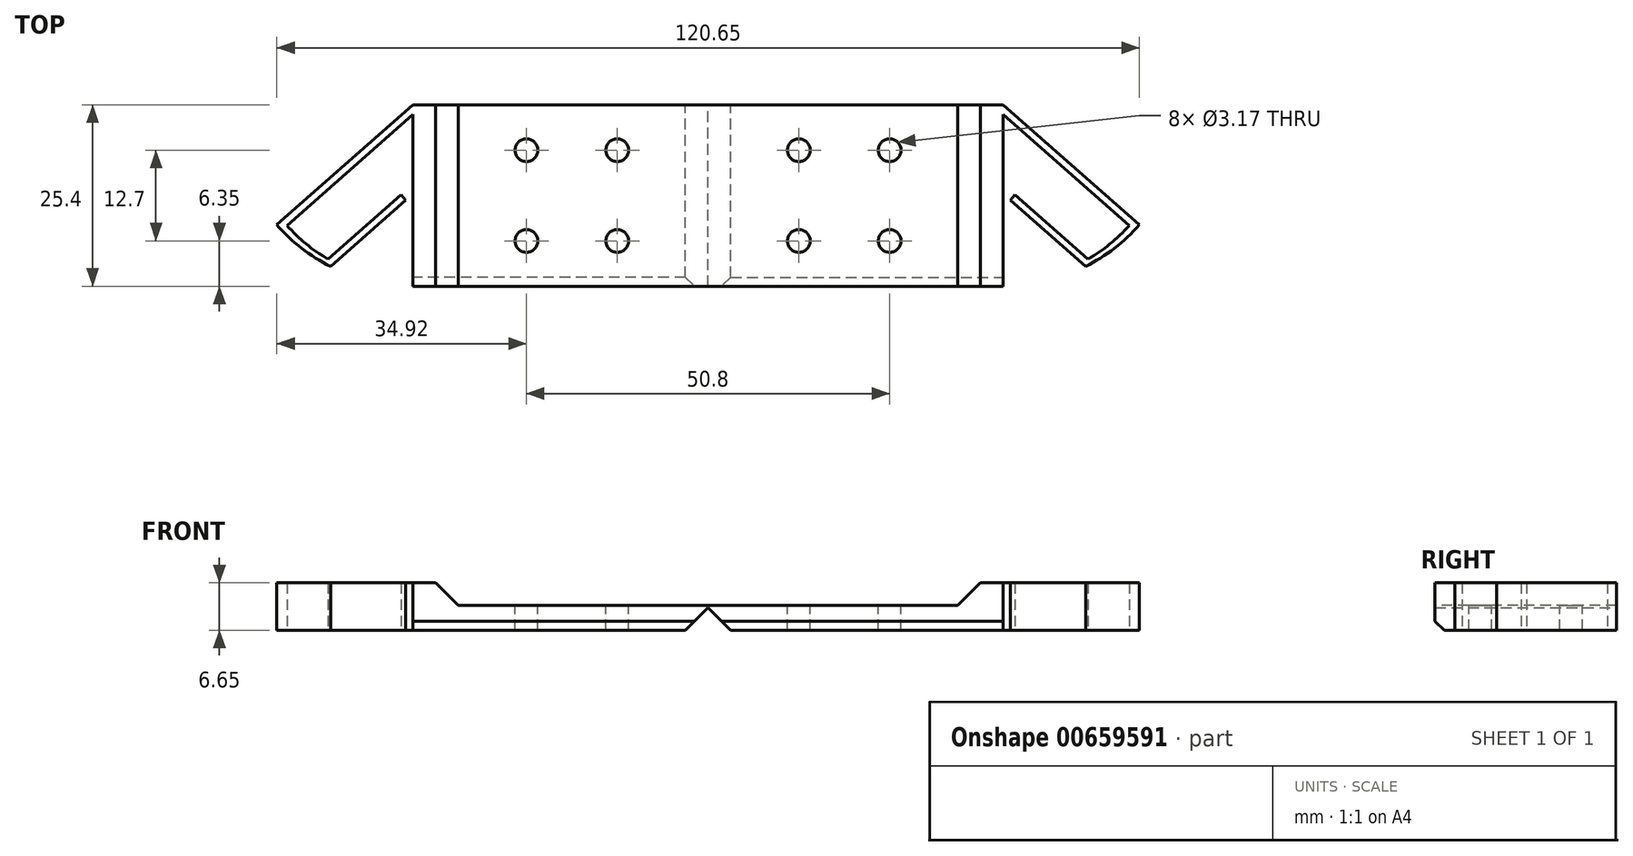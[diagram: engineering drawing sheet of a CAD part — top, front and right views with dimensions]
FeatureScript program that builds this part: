
annotation { "Feature Type Name" : "Feature", "Feature Type Description" : "" }
export const myFeature = defineFeature(function(context is Context, id is Id, definition is map)
    precondition{}
    {
        {
            var Q0;
            Q0=qCreatedBy(makeId("Top.planeOp"),FACE);
            var sketch = newSketch(context, id + "F0", { "sketchPlane" : qUnion([Q0])});
            skLineSegment(sketch, "E0.bottom", {"start": v(28.58, -12.7) * mm, "end": v(-28.58, -12.7) * mm});
            skLineSegment(sketch, "E0.top", {"start": v(28.58, 12.7) * mm, "end": v(-28.58, 12.7) * mm});
            skLineSegment(sketch, "E0.left", {"start": v(28.58, -12.7) * mm, "end": v(28.58, 12.7) * mm});
            skLineSegment(sketch, "E0.right", {"start": v(-28.57, -12.7) * mm, "end": v(-28.57, 12.7) * mm});
            skPoint(sketch, "E0.middle", {"position": v(0, 0) * mm});
            skLineSegment(sketch, "E1", {"start": v(-9.53, 11.37) * mm, "end": v(-9.52, -12.7) * mm});
            skLineSegment(sketch, "E2", {"start": v(0, -12.7) * mm, "end": v(0, 12.7) * mm});
            skPoint(sketch, "E3", {"position": v(-22.22, -12.7) * mm});
            skLineSegment(sketch, "E4", {"start": v(-9.53, 12.7) * mm, "end": v(-28.57, -4.1) * mm});
            skPoint(sketch, "E5", {"position": v(-19.05, -12.7) * mm});
            skArc(sketch, "E6", {"start": v(-28.57, -4.1) * mm, "mid": v(-25.09, -7.37) * mm, "end": v(-21.05, -9.94) * mm});
            skLineSegment(sketch, "E7", {"start": v(-21.05, -9.94) * mm, "end": v(-10.53, -0.66) * mm});
            skLineSegment(sketch, "E8", {"start": v(-10.53, -0.66) * mm, "end": v(-11.19, 0.1) * mm});
            skLineSegment(sketch, "E9", {"start": v(-11.19, 0.1) * mm, "end": v(-11.19, 0.1) * mm});
            skLineSegment(sketch, "E10", {"start": v(-9.53, 11.37) * mm, "end": v(-27.15, -4.18) * mm});
            skArc(sketch, "E11", {"start": v(-27.15, -4.18) * mm, "mid": v(-24.46, -6.77) * mm, "end": v(-21.4, -8.91) * mm});
            skLineSegment(sketch, "E12", {"start": v(-21.4, -8.91) * mm, "end": v(-11.19, 0.1) * mm});
            skSolve(sketch);
        }
        {
            var Q0;
            {var subQ0=sQuery(id+"F0.wireOp",EDGE,"E0.left");Q0=makeQuery(id+"F0.imprint","IMPRINT",FACE,{"disambiguationData":[TD([[makeQuery(id+"F0.imprint","IMPRINT",EDGE,{"derivedFrom":subQ0}),1.0]])]});}
            var Q1;
            {var subQ1=sQuery(id+"F0.wireOp",EDGE,"E1");Q1=makeQuery(id+"F0.imprint","IMPRINT",FACE,{"disambiguationData":[TD([[makeQuery(id+"F0.imprint","IMPRINT",EDGE,{"derivedFrom":subQ1}),1.0]])]});}
            var Q2;
            {var subQ0=sQuery(id+"F0.wireOp",EDGE,"Ll8NUgnO-918t-zldm-zNWz-RsUZQomu35K8");Q2=makeQuery(id+"F0.imprint","IMPRINT",FACE,{"disambiguationData":[TD([[makeQuery(id+"F0.imprint","IMPRINT",EDGE,{"derivedFrom":subQ0}),1.0]])]});}
            extrude(context, id + "F1", {"entities" : qUnion([Q0, Q1, Q2]), "depth" : 3.17 * mm, "offsetDistance" : 25.4 * mm});
        }
        {
            var Q0;
            {var subQ1=sQuery(id+"F0.wireOp",EDGE,"E1");Q0=makeQuery(id+"F0.imprint","IMPRINT",FACE,{"disambiguationData":[TD([[makeQuery(id+"F0.imprint","IMPRINT",EDGE,{"derivedFrom":subQ1}),1.0]])]});}
            extrude(context, id + "F2", {"entities" : qUnion([Q0]), "operationType" : NewBodyOperationType.ADD, "depth" : 6.35 * mm, "offsetDistance" : 25.4 * mm});
        }
        {
            var Q0;
            Q0=makeQuery(id+"F2.opExtrude","CAP_EDGE",EDGE,{"disambiguationData":[OSD([sQuery(id+"F0.wireOp",EDGE,"E2")])],"isStart":false});
            chamfer(context, id + "F3", {"entities" : qUnion([Q0]), "width" : 6.35 * mm, "tangentPropagation" : true});
        }
        {
            var Q0;
            {var subQ0=sQuery(id+"F0.wireOp",EDGE,"E0.left");Q0=makeQuery(id+"F37SAEC6IVc2ddh_1.boolean.opBoolean","MERGE",FACE,{"derivedFrom":[makeQuery(id+"F1.opExtrude","SWEPT_FACE",FACE,{"disambiguationData":[OSD([subQ0])]}),makeQuery(id+"F37SAEC6IVc2ddh_1.opExtrude","SWEPT_FACE",FACE,{"disambiguationData":[OSD([subQ0])]})]});}
            cPlane(context, id + "F4", {"entities" : qUnion([Q0]), "cplaneType" : CPlaneType.OFFSET, "offset" : 3.17 * mm, "width" : 152.4 * mm, "height" : 152.4 * mm});
        }
        {
            var Q0;
            {var subQ0=sQuery(id+"F0.wireOp",EDGE,"E1");Q0=makeQuery(id+"F2.boolean.opBoolean","MERGE",FACE,{"derivedFrom":[makeQuery(id+"F1.opExtrude","SWEPT_FACE",FACE,{"disambiguationData":[OSD([subQ0])]}),makeQuery(id+"F2.opExtrude","SWEPT_FACE",FACE,{"disambiguationData":[OSD([subQ0])]})]});}
            var sketch = newSketch(context, id + "F5", { "sketchPlane" : qUnion([Q0])});
            skLineSegment(sketch, "E13", {"start": v(12.7, 0) * mm, "end": v(12.7, 1.27) * mm});
            skLineSegment(sketch, "E14", {"start": v(12.7, 1.27) * mm, "end": v(11.43, 0) * mm});
            skLineSegment(sketch, "E15", {"start": v(11.43, 0) * mm, "end": v(12.7, 0) * mm});
            skSolve(sketch);
        }
        {
            var Q0;
            {var subQ0=sQuery(id+"F0.wireOp",EDGE,"E0.top");Q0=makeQuery(id+"F2.boolean.opBoolean","MERGE",FACE,{"derivedFrom":[makeQuery(id+"F1.opExtrude","SWEPT_FACE",FACE,{"disambiguationData":[OSD([subQ0])]}),makeQuery(id+"F2.opExtrude","SWEPT_FACE",FACE,{"disambiguationData":[OSD([subQ0])]})]});}
            var sketch = newSketch(context, id + "F6", { "sketchPlane" : qUnion([Q0])});
            skLineSegment(sketch, "E16", {"start": v(-28.58, 3.18) * mm, "end": v(-31.75, 3.18) * mm});
            skLineSegment(sketch, "E17", {"start": v(-31.75, 3.18) * mm, "end": v(-28.58, 0) * mm});
            skLineSegment(sketch, "E18", {"start": v(-28.58, 0) * mm, "end": v(-28.58, 3.18) * mm});
            skSolve(sketch);
        }
        {
            var Q0;
            Q0=makeQuery(id+"F6.imprint","IMPRINT",FACE,{"disambiguationData":[TD([[makeQuery(id+"F6.imprint","IMPRINT",EDGE,{"derivedFrom":sQuery(id+"F6.wireOp",EDGE,"E18")}),1.0]])]});
            var Q1;
            Q1=makeQuery(id+"F6.imprint","IMPRINT",FACE,{"disambiguationData":[TD([[makeQuery(id+"F6.imprint","IMPRINT",EDGE,{"derivedFrom":sQuery(id+"F6.wireOp",EDGE,"E16")}),1.0]])]});
            extrude(context, id + "F7", {"entities" : qUnion([Q0, Q1]), "operationType" : NewBodyOperationType.ADD, "oppositeDirection" : true, "depth" : 25.4 * mm, "offsetDistance" : 25.4 * mm});
        }
        {
            var Q0;
            Q0=makeQuery(id+"F5.imprint","IMPRINT",FACE,{"disambiguationData":[TD([[makeQuery(id+"F5.imprint","IMPRINT",EDGE,{"derivedFrom":sQuery(id+"F5.wireOp",EDGE,"E13")}),-1.0]])]});
            extrude(context, id + "F8", {"entities" : qUnion([Q0]), "operationType" : NewBodyOperationType.REMOVE, "oppositeDirection" : true, "depth" : 50.8 * mm, "offsetDistance" : 25.4 * mm});
        }
        {
            var Q0;
            Q0=makeQuery(id+"F1.opExtrude","SWEPT_BODY",BODY,{"disambiguationData":[OSD([sQuery(id+"F0.wireOp",EDGE,"E0.bottom"),sQuery(id+"F0.wireOp",EDGE,"E0.top"),sQuery(id+"F0.wireOp",EDGE,"E0.left"),sQuery(id+"F0.wireOp",EDGE,"E1"),sQuery(id+"F0.wireOp",EDGE,"E4"),sQuery(id+"F0.wireOp",EDGE,"E6"),sQuery(id+"F0.wireOp",EDGE,"E7"),sQuery(id+"F0.wireOp",EDGE,"E8"),sQuery(id+"F0.wireOp",EDGE,"E10"),sQuery(id+"F0.wireOp",EDGE,"E11"),sQuery(id+"F0.wireOp",EDGE,"E12")])]});
            var Q1;
            Q1=qCreatedBy(id+"F4.planeOp",FACE);
            mirror(context, id + "F9", {"entities" : qUnion([Q0]), "mirrorPlane" : qUnion([Q1])});
        }
        {
            var Q0;
            {var subQ0=sQuery(id+"F0.wireOp",EDGE,"E0.top");Q0=makeQuery(id+"F7.boolean.opBoolean","MERGE",FACE,{"derivedFrom":[makeQuery(id+"F1.opExtrude","CAP_FACE",FACE,{"disambiguationData":[OSD([sQuery(id+"F0.wireOp",EDGE,"E0.bottom"),subQ0,sQuery(id+"F0.wireOp",EDGE,"E0.left"),sQuery(id+"F0.wireOp",EDGE,"E1"),sQuery(id+"F0.wireOp",EDGE,"E4"),sQuery(id+"F0.wireOp",EDGE,"E6"),sQuery(id+"F0.wireOp",EDGE,"E7"),sQuery(id+"F0.wireOp",EDGE,"E8"),sQuery(id+"F0.wireOp",EDGE,"E10"),sQuery(id+"F0.wireOp",EDGE,"E11"),sQuery(id+"F0.wireOp",EDGE,"E12")])],"isStart":false}),makeQuery(id+"F7.opExtrude","SWEPT_FACE",FACE,{"disambiguationData":[OSD([subQ0,sQuery(id+"F6.wireOp",EDGE,"E16")])]})]});}
            var sketch = newSketch(context, id + "F10", { "sketchPlane" : qUnion([Q0])});
            skLineSegment(sketch, "E19", {"start": v(31.75, 0) * mm, "end": v(19.05, 0) * mm, "construction": true});
            skPoint(sketch, "E19.endSnap0", {"position": v(-3.17, 0) * mm});
            skLineSegment(sketch, "E20", {"start": v(19.05, 0) * mm, "end": v(6.35, 0) * mm, "construction": true});
            skLineSegment(sketch, "E21", {"start": v(6.35, 0) * mm, "end": v(6.35, 0) * mm});
            skLineSegment(sketch, "E22", {"start": v(31.75, 0) * mm, "end": v(44.45, 0) * mm, "construction": true});
            skLineSegment(sketch, "E23", {"start": v(44.45, 0) * mm, "end": v(57.15, 0) * mm, "construction": true});
            skLineSegment(sketch, "E24.bottom", {"start": v(44.45, 6.35) * mm, "end": v(19.05, 6.35) * mm, "construction": true});
            skLineSegment(sketch, "E24.top", {"start": v(44.45, -6.35) * mm, "end": v(19.05, -6.35) * mm, "construction": true});
            skLineSegment(sketch, "E24.left", {"start": v(44.45, 6.35) * mm, "end": v(44.45, -6.35) * mm, "construction": true});
            skLineSegment(sketch, "E24.right", {"start": v(19.05, 6.35) * mm, "end": v(19.05, -6.35) * mm, "construction": true});
            skPoint(sketch, "E24.middle", {"position": v(31.75, 0) * mm});
            skLineSegment(sketch, "E25.bottom", {"start": v(57.15, 6.35) * mm, "end": v(6.35, 6.35) * mm, "construction": true});
            skLineSegment(sketch, "E25.top", {"start": v(57.15, -6.35) * mm, "end": v(6.35, -6.35) * mm, "construction": true});
            skLineSegment(sketch, "E25.left", {"start": v(57.15, 6.35) * mm, "end": v(57.15, -6.35) * mm, "construction": true});
            skLineSegment(sketch, "E25.right", {"start": v(6.35, 6.35) * mm, "end": v(6.35, -6.35) * mm, "construction": true});
            skSolve(sketch);
        }
        {
            var Q0;
            Q0=sQuery(id+"F10.wireOp",VERTEX,"E25.left.end");
            var Q1;
            Q1=sQuery(id+"F10.wireOp",VERTEX,"E25.bottom.start");
            var Q2;
            Q2=sQuery(id+"F10.wireOp",VERTEX,"E24.bottom.end");
            var Q3;
            Q3=sQuery(id+"F10.wireOp",VERTEX,"E24.right.end");
            var Q4;
            Q4=sQuery(id+"F10.wireOp",VERTEX,"E25.right.end");
            var Q5;
            Q5=sQuery(id+"F10.wireOp",VERTEX,"E25.bottom.end");
            var Q6;
            Q6=sQuery(id+"F10.wireOp",VERTEX,"E24.top.start");
            var Q7;
            Q7=sQuery(id+"F10.wireOp",VERTEX,"E24.bottom.start");
            var Q8;
            Q8=makeQuery(id+"F1.opExtrude","SWEPT_BODY",BODY,{"disambiguationData":[OSD([sQuery(id+"F0.wireOp",EDGE,"E0.bottom"),sQuery(id+"F0.wireOp",EDGE,"E0.top"),sQuery(id+"F0.wireOp",EDGE,"E0.left"),sQuery(id+"F0.wireOp",EDGE,"E1"),sQuery(id+"F0.wireOp",EDGE,"E4"),sQuery(id+"F0.wireOp",EDGE,"E6"),sQuery(id+"F0.wireOp",EDGE,"E7"),sQuery(id+"F0.wireOp",EDGE,"E8"),sQuery(id+"F0.wireOp",EDGE,"E10"),sQuery(id+"F0.wireOp",EDGE,"E11"),sQuery(id+"F0.wireOp",EDGE,"E12")])]});
            var Q9;
            Q9=makeQuery(id+"F9.opPattern","COPY",BODY,{"derivedFrom":makeQuery(id+"F1.opExtrude","SWEPT_BODY",BODY,{"disambiguationData":[OSD([sQuery(id+"F0.wireOp",EDGE,"E0.bottom"),sQuery(id+"F0.wireOp",EDGE,"E0.top"),sQuery(id+"F0.wireOp",EDGE,"E0.left"),sQuery(id+"F0.wireOp",EDGE,"E1"),sQuery(id+"F0.wireOp",EDGE,"E4"),sQuery(id+"F0.wireOp",EDGE,"E6"),sQuery(id+"F0.wireOp",EDGE,"E7"),sQuery(id+"F0.wireOp",EDGE,"E8"),sQuery(id+"F0.wireOp",EDGE,"E10"),sQuery(id+"F0.wireOp",EDGE,"E11"),sQuery(id+"F0.wireOp",EDGE,"E12")])]}),"instanceName":"1"});
            hole(context, id + "F11", {"style" : HoleStyle.SIMPLE, "endStyle" : HoleEndStyle.THROUGH, "holeDiameter" : 3.17 * mm, "majorDiameter" : 6.35 * mm, "isTappedThrough" : true, "tappedDepth" : 12.7 * mm, "tapClearance" : 3, "locations" : qUnion([Q0, Q1, Q2, Q3, Q4, Q5, Q6, Q7]), "scope" : qUnion([Q8, Q9])});
        }
        {
            var Q0;
            {var subQ0=sQuery(id+"F0.wireOp",EDGE,"E0.top");Q0=makeQuery(id+"F7.boolean.opBoolean","MERGE",FACE,{"derivedFrom":[makeQuery(id+"F1.opExtrude","CAP_FACE",FACE,{"disambiguationData":[OSD([sQuery(id+"F0.wireOp",EDGE,"E0.bottom"),subQ0,sQuery(id+"F0.wireOp",EDGE,"E0.left"),sQuery(id+"F0.wireOp",EDGE,"E1"),sQuery(id+"F0.wireOp",EDGE,"E4"),sQuery(id+"F0.wireOp",EDGE,"E6"),sQuery(id+"F0.wireOp",EDGE,"E7"),sQuery(id+"F0.wireOp",EDGE,"E8"),sQuery(id+"F0.wireOp",EDGE,"E10"),sQuery(id+"F0.wireOp",EDGE,"E11"),sQuery(id+"F0.wireOp",EDGE,"E12")])],"isStart":false}),makeQuery(id+"F7.opExtrude","SWEPT_FACE",FACE,{"disambiguationData":[OSD([subQ0,sQuery(id+"F6.wireOp",EDGE,"E16")])]})]});}
            var Q1;
            {var subQ0=sQuery(id+"F0.wireOp",EDGE,"E0.top");Q1=makeQuery(id+"F9.opPattern","COPY",FACE,{"derivedFrom":makeQuery(id+"F7.boolean.opBoolean","MERGE",FACE,{"derivedFrom":[makeQuery(id+"F1.opExtrude","CAP_FACE",FACE,{"disambiguationData":[OSD([sQuery(id+"F0.wireOp",EDGE,"E0.bottom"),subQ0,sQuery(id+"F0.wireOp",EDGE,"E0.left"),sQuery(id+"F0.wireOp",EDGE,"E1"),sQuery(id+"F0.wireOp",EDGE,"E4"),sQuery(id+"F0.wireOp",EDGE,"E6"),sQuery(id+"F0.wireOp",EDGE,"E7"),sQuery(id+"F0.wireOp",EDGE,"E8"),sQuery(id+"F0.wireOp",EDGE,"E10"),sQuery(id+"F0.wireOp",EDGE,"E11"),sQuery(id+"F0.wireOp",EDGE,"E12")])],"isStart":false}),makeQuery(id+"F7.opExtrude","SWEPT_FACE",FACE,{"disambiguationData":[OSD([subQ0,sQuery(id+"F6.wireOp",EDGE,"E16")])]})]}),"instanceName":"1"});}
            var Q2;
            Q2=makeQuery(id+"F9.opPattern","COPY",FACE,{"derivedFrom":makeQuery(id+"F3.opChamfer","BLEND_FACE",FACE,{"disambiguationData":[OSD([sQuery(id+"F0.wireOp",EDGE,"E2")])]}),"instanceName":"1"});
            var Q3;
            Q3=makeQuery(id+"F3.opChamfer","BLEND_FACE",FACE,{"disambiguationData":[OSD([sQuery(id+"F0.wireOp",EDGE,"E2")])]});
            var Q4;
            Q4=makeQuery(id+"F2.opExtrude","CAP_FACE",FACE,{"disambiguationData":[OSD([sQuery(id+"F0.wireOp",EDGE,"E0.bottom"),sQuery(id+"F0.wireOp",EDGE,"E0.top"),sQuery(id+"F0.wireOp",EDGE,"E1"),sQuery(id+"F0.wireOp",EDGE,"E2"),sQuery(id+"F0.wireOp",EDGE,"E4"),sQuery(id+"F0.wireOp",EDGE,"E6"),sQuery(id+"F0.wireOp",EDGE,"E7"),sQuery(id+"F0.wireOp",EDGE,"E8"),sQuery(id+"F0.wireOp",EDGE,"E10"),sQuery(id+"F0.wireOp",EDGE,"E11"),sQuery(id+"F0.wireOp",EDGE,"E12")])],"isStart":false});
            var Q5;
            Q5=makeQuery(id+"F9.opPattern","COPY",FACE,{"derivedFrom":makeQuery(id+"F2.opExtrude","CAP_FACE",FACE,{"disambiguationData":[OSD([sQuery(id+"F0.wireOp",EDGE,"E0.bottom"),sQuery(id+"F0.wireOp",EDGE,"E0.top"),sQuery(id+"F0.wireOp",EDGE,"E1"),sQuery(id+"F0.wireOp",EDGE,"E2"),sQuery(id+"F0.wireOp",EDGE,"E4"),sQuery(id+"F0.wireOp",EDGE,"E6"),sQuery(id+"F0.wireOp",EDGE,"E7"),sQuery(id+"F0.wireOp",EDGE,"E8"),sQuery(id+"F0.wireOp",EDGE,"E10"),sQuery(id+"F0.wireOp",EDGE,"E11"),sQuery(id+"F0.wireOp",EDGE,"E12")])],"isStart":false}),"instanceName":"1"});
            extrude(context, id + "F12", {"entities" : qUnion([Q0, Q1, Q2, Q3, Q4, Q5]), "operationType" : NewBodyOperationType.ADD, "depth" : .3 * mm, "offsetDistance" : 25.4 * mm});
        }
    });
